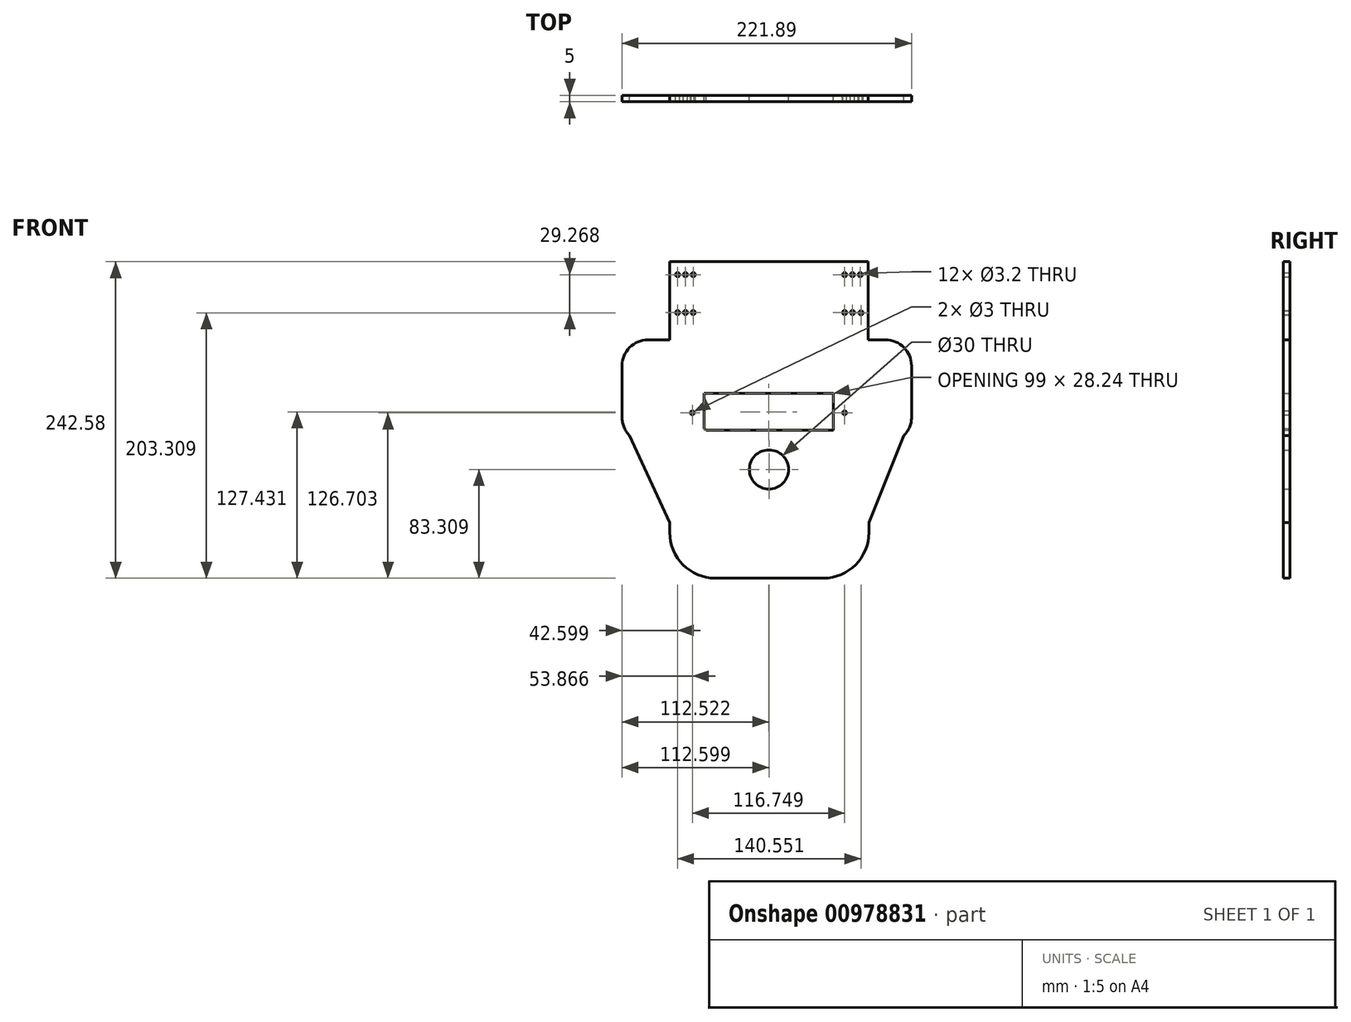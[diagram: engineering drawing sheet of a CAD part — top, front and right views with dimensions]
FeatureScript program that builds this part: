
annotation { "Feature Type Name" : "Feature", "Feature Type Description" : "" }
export const myFeature = defineFeature(function(context is Context, id is Id, definition is map)
    precondition{}
    {
        {
            var Q0;
            Q0=qCreatedBy(makeId("Front.planeOp"),FACE);
            var sketch = newSketch(context, id + "F0", { "sketchPlane" : qUnion([Q0])});
            skLineSegment(sketch, "E0.bottom", {"start": v(-87.28, 93.42) * mm, "end": v(64.72, 93.42) * mm});
            skLineSegment(sketch, "E0.top", {"start": v(-87.28, -106.58) * mm, "end": v(64.72, -106.58) * mm});
            skLineSegment(sketch, "E0.left", {"start": v(-87.28, 93.42) * mm, "end": v(-87.28, -106.58) * mm});
            skLineSegment(sketch, "E0.right", {"start": v(64.72, 93.42) * mm, "end": v(64.72, -106.58) * mm});
            skCircle(sketch, "E1", {"center": v(-81.28, 83.42) * mm, "radius": 1.6 * mm});
            skCircle(sketch, "E2.0.1.0", {"center": v(-81.28, 54.42) * mm, "radius": 1.6 * mm});
            skCircle(sketch, "E2.1.0.0", {"center": v(-75.28, 83.42) * mm, "radius": 1.6 * mm});
            skCircle(sketch, "E2.1.1.0", {"center": v(-75.28, 54.42) * mm, "radius": 1.6 * mm});
            skCircle(sketch, "E2.2.0.0", {"center": v(-69.28, 83.42) * mm, "radius": 1.6 * mm});
            skCircle(sketch, "E2.2.1.0", {"center": v(-69.28, 54.42) * mm, "radius": 1.6 * mm});
            skLineSegment(sketch, "E2.direction1", {"start": v(-81.28, 83.42) * mm, "end": v(-75.28, 83.42) * mm, "construction": true});
            skCircle(sketch, "E3", {"center": v(58.72, 83.42) * mm, "radius": 1.6 * mm});
            skCircle(sketch, "E4.0.1.0", {"center": v(59.27, 54.15) * mm, "radius": 1.6 * mm});
            skCircle(sketch, "E4.1.0.0", {"center": v(52.72, 83.42) * mm, "radius": 1.6 * mm});
            skCircle(sketch, "E4.1.1.0", {"center": v(52.72, 54.42) * mm, "radius": 1.6 * mm});
            skCircle(sketch, "E4.2.0.0", {"center": v(46.72, 83.42) * mm, "radius": 1.6 * mm});
            skCircle(sketch, "E4.2.1.0", {"center": v(46.72, 54.42) * mm, "radius": 1.6 * mm});
            skLineSegment(sketch, "E4.direction1", {"start": v(58.72, 83.42) * mm, "end": v(52.72, 83.42) * mm, "construction": true});
            skLineSegment(sketch, "E5.top", {"start": v(-87.28, -106.58) * mm, "end": v(-7.39, -106.58) * mm});
            skLineSegment(sketch, "E5.left", {"start": v(-87.28, -52.85) * mm, "end": v(-87.28, -106.58) * mm});
            skCircle(sketch, "E6", {"center": v(-11.28, -65.85) * mm, "radius": 15 * mm});
            skLineSegment(sketch, "E7", {"start": v(-59.35, -35.85) * mm, "end": v(39.65, -35.85) * mm});
            skLineSegment(sketch, "E8", {"start": v(39.65, -35.85) * mm, "end": v(53.02, -20.97) * mm});
            skLineSegment(sketch, "E9", {"start": v(53.02, -20.97) * mm, "end": v(38.14, -7.6) * mm});
            skLineSegment(sketch, "E10", {"start": v(-59.35, -35.85) * mm, "end": v(-74.23, -22.48) * mm});
            skLineSegment(sketch, "E11", {"start": v(-74.23, -22.48) * mm, "end": v(-60.86, -7.6) * mm});
            skLineSegment(sketch, "E12", {"start": v(-60.86, -7.6) * mm, "end": v(38.14, -7.6) * mm});
            skLineSegment(sketch, "E13.bottom", {"start": v(-103.88, 33.5) * mm, "end": v(-87.28, 33.5) * mm});
            skLineSegment(sketch, "E13.top", {"start": v(-103.88, -45.73) * mm, "end": v(-87.28, -45.73) * mm});
            skLineSegment(sketch, "E13.left", {"start": v(-123.88, 13.5) * mm, "end": v(-123.88, -25.73) * mm});
            skLineSegment(sketch, "E13.right", {"start": v(-87.28, 33.5) * mm, "end": v(-87.28, -45.73) * mm});
            skLineSegment(sketch, "E14.bottom", {"start": v(64.72, 33.5) * mm, "end": v(78, 33.5) * mm});
            skLineSegment(sketch, "E14.top", {"start": v(64.72, -45.73) * mm, "end": v(78, -45.73) * mm});
            skLineSegment(sketch, "E14.left", {"start": v(64.72, 33.5) * mm, "end": v(64.72, -45.73) * mm});
            skLineSegment(sketch, "E14.right", {"start": v(98, 13.5) * mm, "end": v(98, -25.73) * mm});
            skPoint(sketch, "E15.visualSharp", {"position": v(-123.88, 33.5) * mm});
            skArc(sketch, "E15.filletArc", {"start": v(-103.88, 33.5) * mm, "mid": v(-118.02, 27.65) * mm, "end": v(-123.88, 13.5) * mm});
            skPoint(sketch, "E16.visualSharp", {"position": v(-123.88, -45.73) * mm});
            skArc(sketch, "E16.filletArc", {"start": v(-123.88, -25.73) * mm, "mid": v(-118.02, -39.87) * mm, "end": v(-103.88, -45.73) * mm});
            skPoint(sketch, "E17.visualSharp", {"position": v(98, 33.5) * mm});
            skArc(sketch, "E17.filletArc", {"start": v(98, 13.5) * mm, "mid": v(92.15, 27.65) * mm, "end": v(78, 33.5) * mm});
            skPoint(sketch, "E18.visualSharp", {"position": v(98, -45.73) * mm});
            skArc(sketch, "E18.filletArc", {"start": v(78, -45.73) * mm, "mid": v(92.15, -39.87) * mm, "end": v(98, -25.73) * mm});
            skLineSegment(sketch, "E19", {"start": v(-60.86, -7.6) * mm, "end": v(-60.86, -35.85) * mm});
            skLineSegment(sketch, "E20", {"start": v(38.14, -7.6) * mm, "end": v(38.14, -35.85) * mm});
            skLineSegment(sketch, "E21.bottom", {"start": v(-87.28, -106.58) * mm, "end": v(65.31, -106.58) * mm});
            skLineSegment(sketch, "E21.top", {"start": v(-52.28, -149.16) * mm, "end": v(30.31, -149.16) * mm});
            skLineSegment(sketch, "E21.left", {"start": v(-87.28, -106.58) * mm, "end": v(-87.28, -114.16) * mm});
            skLineSegment(sketch, "E21.right", {"start": v(65.31, -106.58) * mm, "end": v(65.31, -114.16) * mm});
            skPoint(sketch, "E22.visualSharp", {"position": v(65.31, -149.16) * mm});
            skArc(sketch, "E22.filletArc", {"start": v(62.7, -149.16) * mm, "mid": v(64.55, -148.4) * mm, "end": v(65.31, -146.55) * mm});
            skPoint(sketch, "E23.visualSharp", {"position": v(-87.28, -149.16) * mm});
            skArc(sketch, "E23.filletArc", {"start": v(-87.28, -114.16) * mm, "mid": v(-77.03, -138.9) * mm, "end": v(-52.28, -149.16) * mm});
            skArc(sketch, "E24.filletArc", {"start": v(30.31, -149.16) * mm, "mid": v(55.06, -138.9) * mm, "end": v(65.31, -114.16) * mm});
            skLineSegment(sketch, "E25", {"start": v(-118.02, -39.87) * mm, "end": v(-87.28, -106.58) * mm});
            skLineSegment(sketch, "E26", {"start": v(92.15, -39.87) * mm, "end": v(65.31, -106.58) * mm});
            skCircle(sketch, "E27", {"center": v(-70.01, -22.46) * mm, "radius": 1.5 * mm});
            skCircle(sketch, "E28", {"center": v(46.74, -22.46) * mm, "radius": 1.5 * mm});
            skSolve(sketch);
        }
        {
            var Q0;
            {var subQ0=sQuery(id+"F0.wireOp",EDGE,"E8");Q0=makeQuery(id+"F0.imprint","IMPRINT",FACE,{"disambiguationData":[TD([[makeQuery(id+"F0.imprint","IMPRINT",EDGE,{"derivedFrom":subQ0}),1.0]])]});}
            var Q1;
            {var subQ3=sQuery(id+"F0.wireOp",EDGE,"E11");Q1=makeQuery(id+"F0.imprint","IMPRINT",FACE,{"disambiguationData":[TD([[makeQuery(id+"F0.imprint","IMPRINT",EDGE,{"derivedFrom":subQ3}),-1.0]])]});}
            var Q2;
            {var subQ8=sQuery(id+"F0.wireOp",EDGE,"E0.bottom");Q2=makeQuery(id+"F0.imprint","IMPRINT",FACE,{"disambiguationData":[TD([[makeQuery(id+"F0.imprint","IMPRINT",EDGE,{"derivedFrom":subQ8}),-1.0]])]});}
            var Q3;
            {var subQ2=sQuery(id+"F0.wireOp",EDGE,"E14.bottom");Q3=makeQuery(id+"F0.imprint","IMPRINT",FACE,{"disambiguationData":[TD([[makeQuery(id+"F0.imprint","IMPRINT",EDGE,{"derivedFrom":subQ2}),-1.0]])]});}
            var Q4;
            {var subQ1=sQuery(id+"F0.wireOp",EDGE,"E13.bottom");Q4=makeQuery(id+"F0.imprint","IMPRINT",FACE,{"disambiguationData":[TD([[makeQuery(id+"F0.imprint","IMPRINT",EDGE,{"derivedFrom":subQ1}),-1.0]])]});}
            var Q5;
            {var subQ1=sQuery(id+"F0.wireOp",EDGE,"E13.top");Q5=makeQuery(id+"F0.imprint","IMPRINT",FACE,{"disambiguationData":[TD([[makeQuery(id+"F0.imprint","IMPRINT",EDGE,{"derivedFrom":subQ1}),-1.0]])]});}
            var Q6;
            {var subQ1=sQuery(id+"F0.wireOp",EDGE,"E14.top");Q6=makeQuery(id+"F0.imprint","IMPRINT",FACE,{"disambiguationData":[TD([[makeQuery(id+"F0.imprint","IMPRINT",EDGE,{"derivedFrom":subQ1}),-1.0]])]});}
            var Q7;
            {var subQ0=sQuery(id+"F0.wireOp",EDGE,"E21.bottom");Q7=makeQuery(id+"F0.imprint","IMPRINT",FACE,{"disambiguationData":[TD([[makeQuery(id+"F0.imprint","IMPRINT",EDGE,{"derivedFrom":subQ0}),-1.0]])]});}
            extrude(context, id + "F1", {"entities" : qUnion([Q0, Q1, Q2, Q3, Q4, Q5, Q6, Q7]), "depth" : 5 * mm, "offsetDistance" : 25 * mm});
        }
    });
